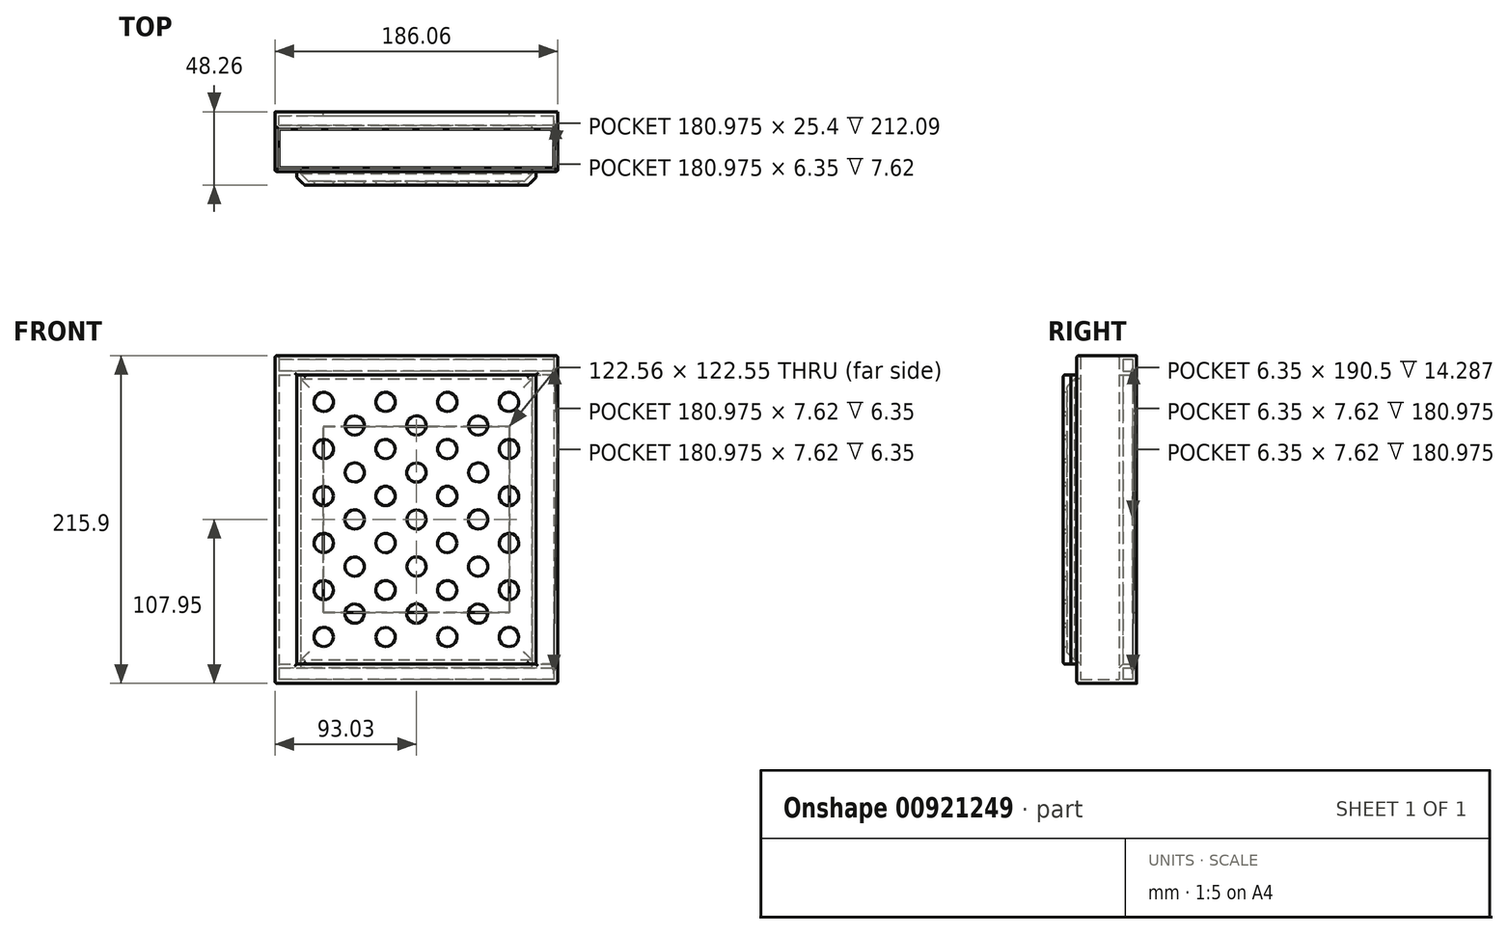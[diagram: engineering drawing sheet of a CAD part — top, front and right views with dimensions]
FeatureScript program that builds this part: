
annotation { "Feature Type Name" : "Feature", "Feature Type Description" : "" }
export const myFeature = defineFeature(function(context is Context, id is Id, definition is map)
    precondition{}
    {
        {
            var Q0;
            Q0=qCreatedBy(makeId("Top.planeOp"),FACE);
            var sketch = newSketch(context, id + "F0", { "sketchPlane" : qUnion([Q0])});
            skLineSegment(sketch, "E0.left", {"start": v(-93.03, 45.72) * mm, "end": v(-93.03, 34.29) * mm});
            skLineSegment(sketch, "E0.right", {"start": v(93.03, 45.72) * mm, "end": v(93.03, 34.29) * mm});
            skLineSegment(sketch, "E1.bottom", {"start": v(-93.03, 34.29) * mm, "end": v(-90.49, 34.29) * mm});
            skLineSegment(sketch, "E1.top", {"start": v(-93.03, 6.35) * mm, "end": v(-90.49, 6.35) * mm});
            skLineSegment(sketch, "E1.left", {"start": v(-93.03, 34.29) * mm, "end": v(-93.03, 6.35) * mm});
            skLineSegment(sketch, "E1.right", {"start": v(-90.49, 34.29) * mm, "end": v(-90.49, 6.35) * mm});
            skLineSegment(sketch, "E2.bottom", {"start": v(93.03, 34.29) * mm, "end": v(90.49, 34.29) * mm});
            skLineSegment(sketch, "E2.top", {"start": v(93.03, 6.35) * mm, "end": v(90.49, 6.35) * mm});
            skLineSegment(sketch, "E2.left", {"start": v(93.03, 34.29) * mm, "end": v(93.03, 6.35) * mm});
            skLineSegment(sketch, "E2.right", {"start": v(90.49, 34.29) * mm, "end": v(90.49, 6.35) * mm});
            skLineSegment(sketch, "E3.bottom", {"start": v(-90.49, 6.35) * mm, "end": v(-76.2, 6.35) * mm});
            skLineSegment(sketch, "E3.top", {"start": v(-90.49, 8.89) * mm, "end": v(-76.2, 8.89) * mm});
            skLineSegment(sketch, "E3.left", {"start": v(-90.49, 6.35) * mm, "end": v(-90.49, 8.89) * mm});
            skLineSegment(sketch, "E3.right", {"start": v(-76.2, 6.35) * mm, "end": v(-76.2, 8.89) * mm});
            skLineSegment(sketch, "E4.bottom", {"start": v(90.49, 6.35) * mm, "end": v(76.2, 6.35) * mm});
            skLineSegment(sketch, "E4.top", {"start": v(90.49, 8.89) * mm, "end": v(76.2, 8.89) * mm});
            skLineSegment(sketch, "E4.left", {"start": v(90.49, 6.35) * mm, "end": v(90.49, 8.89) * mm});
            skLineSegment(sketch, "E4.right", {"start": v(76.2, 6.35) * mm, "end": v(76.2, 8.89) * mm});
            skLineSegment(sketch, "E5", {"start": v(-93.03, 45.72) * mm, "end": v(93.03, 45.72) * mm});
            skLineSegment(sketch, "E6.bottom", {"start": v(-93.03, 34.29) * mm, "end": v(-76.2, 34.29) * mm});
            skLineSegment(sketch, "E6.top", {"start": v(-93.03, 36.83) * mm, "end": v(-76.2, 36.83) * mm});
            skLineSegment(sketch, "E6.left", {"start": v(-93.03, 34.29) * mm, "end": v(-93.03, 36.83) * mm});
            skLineSegment(sketch, "E6.right", {"start": v(-76.2, 34.29) * mm, "end": v(-76.2, 36.83) * mm});
            skLineSegment(sketch, "E7.bottom", {"start": v(93.03, 34.29) * mm, "end": v(76.2, 34.29) * mm});
            skLineSegment(sketch, "E7.top", {"start": v(93.03, 36.83) * mm, "end": v(76.2, 36.83) * mm});
            skLineSegment(sketch, "E7.left", {"start": v(93.03, 34.29) * mm, "end": v(93.03, 36.83) * mm});
            skLineSegment(sketch, "E7.right", {"start": v(76.2, 34.29) * mm, "end": v(76.2, 36.83) * mm});
            skLineSegment(sketch, "E8.bottom", {"start": v(-93.03, 36.83) * mm, "end": v(-90.49, 36.83) * mm});
            skLineSegment(sketch, "E8.top", {"start": v(-93.03, 45.72) * mm, "end": v(-90.49, 45.72) * mm});
            skLineSegment(sketch, "E8.left", {"start": v(-93.03, 36.83) * mm, "end": v(-93.03, 45.72) * mm});
            skLineSegment(sketch, "E8.right", {"start": v(-90.49, 36.83) * mm, "end": v(-90.49, 45.72) * mm});
            skLineSegment(sketch, "E9.bottom", {"start": v(93.03, 36.83) * mm, "end": v(90.49, 36.83) * mm});
            skLineSegment(sketch, "E9.top", {"start": v(93.03, 45.72) * mm, "end": v(90.49, 45.72) * mm});
            skLineSegment(sketch, "E9.left", {"start": v(93.03, 36.83) * mm, "end": v(93.03, 45.72) * mm});
            skLineSegment(sketch, "E9.right", {"start": v(90.49, 36.83) * mm, "end": v(90.49, 45.72) * mm});
            skLineSegment(sketch, "E10.top", {"start": v(-93.03, 43.18) * mm, "end": v(93.03, 43.18) * mm});
            skLineSegment(sketch, "E10.left", {"start": v(-93.03, 45.72) * mm, "end": v(-93.03, 43.18) * mm});
            skLineSegment(sketch, "E10.right", {"start": v(93.03, 45.72) * mm, "end": v(93.03, 43.18) * mm});
            skLineSegment(sketch, "E11.bottom", {"start": v(-76.2, 6.35) * mm, "end": v(-78.74, 6.35) * mm});
            skLineSegment(sketch, "E11.top", {"start": v(-76.2, -2.54) * mm, "end": v(-78.74, -2.54) * mm});
            skLineSegment(sketch, "E11.left", {"start": v(-76.2, 6.35) * mm, "end": v(-76.2, -2.54) * mm});
            skLineSegment(sketch, "E11.right", {"start": v(-78.74, 6.35) * mm, "end": v(-78.74, -2.54) * mm});
            skLineSegment(sketch, "E12.bottom", {"start": v(76.2, 6.35) * mm, "end": v(78.74, 6.35) * mm});
            skLineSegment(sketch, "E12.top", {"start": v(76.2, -2.54) * mm, "end": v(78.74, -2.54) * mm});
            skLineSegment(sketch, "E12.left", {"start": v(76.2, 6.35) * mm, "end": v(76.2, -2.54) * mm});
            skLineSegment(sketch, "E12.right", {"start": v(78.74, 6.35) * mm, "end": v(78.74, -2.54) * mm});
            skLineSegment(sketch, "E13.bottom", {"start": v(-76.2, -2.54) * mm, "end": v(76.2, -2.54) * mm});
            skLineSegment(sketch, "E13.top", {"start": v(-76.2, 0) * mm, "end": v(76.2, 0) * mm});
            skLineSegment(sketch, "E13.left", {"start": v(-76.2, -2.54) * mm, "end": v(-76.2, 0) * mm});
            skLineSegment(sketch, "E13.right", {"start": v(76.2, -2.54) * mm, "end": v(76.2, 0) * mm});
            skPoint(sketch, "E14", {"position": v(0, 0) * mm});
            skLineSegment(sketch, "E15.bottom", {"start": v(-76.2, 36.83) * mm, "end": v(-78.74, 36.83) * mm});
            skLineSegment(sketch, "E15.top", {"start": v(-76.2, 45.72) * mm, "end": v(-78.74, 45.72) * mm});
            skLineSegment(sketch, "E15.left", {"start": v(-76.2, 36.83) * mm, "end": v(-76.2, 45.72) * mm});
            skLineSegment(sketch, "E15.right", {"start": v(-78.74, 36.83) * mm, "end": v(-78.74, 45.72) * mm});
            skLineSegment(sketch, "E16.bottom", {"start": v(76.2, 36.83) * mm, "end": v(78.74, 36.83) * mm});
            skLineSegment(sketch, "E16.top", {"start": v(76.2, 45.72) * mm, "end": v(78.74, 45.72) * mm});
            skLineSegment(sketch, "E16.left", {"start": v(76.2, 36.83) * mm, "end": v(76.2, 45.72) * mm});
            skLineSegment(sketch, "E16.right", {"start": v(78.74, 36.83) * mm, "end": v(78.74, 45.72) * mm});
            skSolve(sketch);
        }
        {
            var Q0;
            Q0 = qSketchRegion(id + "F0", true);
            var Q1;
            {var subQ5=sQuery(id+"F0.wireOp",EDGE,"E16.bottom");Q1=makeQuery(id+"F0.imprint","IMPRINT",FACE,{"disambiguationData":[TD([[makeQuery(id+"F0.imprint","IMPRINT",EDGE,{"derivedFrom":subQ5}),1.0]])]});}
            var Q2;
            {var subQ5=sQuery(id+"F0.wireOp",EDGE,"E15.bottom");Q2=makeQuery(id+"F0.imprint","IMPRINT",FACE,{"disambiguationData":[TD([[makeQuery(id+"F0.imprint","IMPRINT",EDGE,{"derivedFrom":subQ5}),-1.0]])]});}
            extrude(context, id + "F1", {"entities" : qUnion([Q0, Q1, Q2]), "depth" : 215.9 * mm, "offsetDistance" : 25.4 * mm});
        }
        {
            var Q0;
            Q0=makeQuery(id+"F1.opExtrude","SWEPT_FACE",FACE,{"disambiguationData":[OSD([sQuery(id+"F0.wireOp",EDGE,"E5")])]});
            var sketch = newSketch(context, id + "F2", { "sketchPlane" : qUnion([Q0])});
            skPoint(sketch, "E17.centerSnap0", {"position": v(93.03, 107.95) * mm});
            skLineSegment(sketch, "E18.bottom", {"start": v(-61.28, 169.23) * mm, "end": v(61.28, 169.23) * mm});
            skLineSegment(sketch, "E18.top", {"start": v(-61.28, 46.67) * mm, "end": v(61.28, 46.67) * mm});
            skLineSegment(sketch, "E18.left", {"start": v(-61.28, 169.23) * mm, "end": v(-61.28, 46.67) * mm});
            skLineSegment(sketch, "E18.right", {"start": v(61.28, 169.23) * mm, "end": v(61.28, 46.67) * mm});
            skPoint(sketch, "E18.middle", {"position": v(0, 107.95) * mm});
            skSolve(sketch);
        }
        {
            var Q0;
            Q0 = qSketchRegion(id + "F2", true);
            extrude(context, id + "F3", {"entities" : qUnion([Q0]), "operationType" : NewBodyOperationType.REMOVE, "endBound" : BoundingType.UP_TO_NEXT, "oppositeDirection" : true, "depth" : 25.4 * mm, "offsetDistance" : 25.4 * mm});
        }
        {
            var Q0;
            Q0=makeQuery(id+"F1.opExtrude","SWEPT_FACE",FACE,{"disambiguationData":[OSD([sQuery(id+"F0.wireOp",EDGE,"E1.left"),sQuery(id+"F0.wireOp",EDGE,"E6.left"),sQuery(id+"F0.wireOp",EDGE,"E8.left"),sQuery(id+"F0.wireOp",EDGE,"E10.left")])]});
            var sketch = newSketch(context, id + "F4", { "sketchPlane" : qUnion([Q0])});
            skLineSegment(sketch, "E19.bottom", {"start": v(-45.72, 215.9) * mm, "end": v(-34.29, 215.9) * mm});
            skLineSegment(sketch, "E19.top", {"start": v(-45.72, 213.36) * mm, "end": v(-34.29, 213.36) * mm});
            skLineSegment(sketch, "E19.left", {"start": v(-45.72, 215.9) * mm, "end": v(-45.72, 213.36) * mm});
            skLineSegment(sketch, "E19.right", {"start": v(-34.29, 215.9) * mm, "end": v(-34.29, 213.36) * mm});
            skLineSegment(sketch, "E20.bottom", {"start": v(-45.72, 0) * mm, "end": v(-6.35, 0) * mm});
            skLineSegment(sketch, "E20.top", {"start": v(-45.72, 2.54) * mm, "end": v(-6.35, 2.54) * mm});
            skLineSegment(sketch, "E20.left", {"start": v(-45.72, 0) * mm, "end": v(-45.72, 2.54) * mm});
            skLineSegment(sketch, "E20.right", {"start": v(-6.35, 0) * mm, "end": v(-6.35, 2.54) * mm});
            skLineSegment(sketch, "E21.bottom", {"start": v(-6.35, 215.9) * mm, "end": v(-8.89, 215.9) * mm});
            skLineSegment(sketch, "E21.top", {"start": v(-6.35, 203.2) * mm, "end": v(-8.89, 203.2) * mm});
            skLineSegment(sketch, "E21.left", {"start": v(-6.35, 215.9) * mm, "end": v(-6.35, 203.2) * mm});
            skLineSegment(sketch, "E21.right", {"start": v(-8.89, 215.9) * mm, "end": v(-8.89, 203.2) * mm});
            skLineSegment(sketch, "E22.bottom", {"start": v(-6.35, 0) * mm, "end": v(-8.89, 0) * mm});
            skLineSegment(sketch, "E22.top", {"start": v(-6.35, 12.7) * mm, "end": v(-8.89, 12.7) * mm});
            skLineSegment(sketch, "E22.left", {"start": v(-6.35, 0) * mm, "end": v(-6.35, 12.7) * mm});
            skLineSegment(sketch, "E22.right", {"start": v(-8.89, 0) * mm, "end": v(-8.89, 12.7) * mm});
            skLineSegment(sketch, "E23.bottom", {"start": v(-34.29, 215.9) * mm, "end": v(-36.83, 215.9) * mm});
            skLineSegment(sketch, "E23.top", {"start": v(-34.29, 203.2) * mm, "end": v(-36.83, 203.2) * mm});
            skLineSegment(sketch, "E23.left", {"start": v(-34.29, 215.9) * mm, "end": v(-34.29, 203.2) * mm});
            skLineSegment(sketch, "E23.right", {"start": v(-36.83, 215.9) * mm, "end": v(-36.83, 203.2) * mm});
            skLineSegment(sketch, "E24.bottom", {"start": v(-34.29, 0) * mm, "end": v(-36.83, 0) * mm});
            skLineSegment(sketch, "E24.top", {"start": v(-34.29, 12.7) * mm, "end": v(-36.83, 12.7) * mm});
            skLineSegment(sketch, "E24.left", {"start": v(-34.29, 0) * mm, "end": v(-34.29, 12.7) * mm});
            skLineSegment(sketch, "E24.right", {"start": v(-36.83, 0) * mm, "end": v(-36.83, 12.7) * mm});
            skLineSegment(sketch, "E25.bottom", {"start": v(-36.83, 203.2) * mm, "end": v(-45.72, 203.2) * mm});
            skLineSegment(sketch, "E25.top", {"start": v(-36.83, 205.74) * mm, "end": v(-45.72, 205.74) * mm});
            skLineSegment(sketch, "E25.left", {"start": v(-36.83, 203.2) * mm, "end": v(-36.83, 205.74) * mm});
            skLineSegment(sketch, "E25.right", {"start": v(-45.72, 203.2) * mm, "end": v(-45.72, 205.74) * mm});
            skLineSegment(sketch, "E26.bottom", {"start": v(-36.83, 12.7) * mm, "end": v(-45.72, 12.7) * mm});
            skLineSegment(sketch, "E26.top", {"start": v(-36.83, 10.16) * mm, "end": v(-45.72, 10.16) * mm});
            skLineSegment(sketch, "E26.left", {"start": v(-36.83, 12.7) * mm, "end": v(-36.83, 10.16) * mm});
            skLineSegment(sketch, "E26.right", {"start": v(-45.72, 12.7) * mm, "end": v(-45.72, 10.16) * mm});
            skSolve(sketch);
        }
        {
            var Q0;
            Q0 = qSketchRegion(id + "F4", true);
            var Q1;
            Q1=makeQuery(id+"F1.opExtrude","SWEPT_FACE",FACE,{"disambiguationData":[OSD([sQuery(id+"F0.wireOp",EDGE,"E2.left"),sQuery(id+"F0.wireOp",EDGE,"E7.left"),sQuery(id+"F0.wireOp",EDGE,"E9.left"),sQuery(id+"F0.wireOp",EDGE,"E10.right")])]});
            extrude(context, id + "F5", {"entities" : qUnion([Q0]), "operationType" : NewBodyOperationType.ADD, "endBound" : BoundingType.UP_TO_SURFACE, "oppositeDirection" : true, "depth" : 25.4 * mm, "endBoundEntityFace" : qUnion([Q1]), "offsetDistance" : 25.4 * mm});
        }
        {
            var Q0;
            Q0=makeQuery(id+"F1.opExtrude","SWEPT_FACE",FACE,{"disambiguationData":[OSD([sQuery(id+"F0.wireOp",EDGE,"E12.right")])]});
            var sketch = newSketch(context, id + "F6", { "sketchPlane" : qUnion([Q0])});
            skLineSegment(sketch, "E27.bottom", {"start": v(-2.54, 0) * mm, "end": v(6.35, 0) * mm});
            skLineSegment(sketch, "E27.top", {"start": v(-2.54, 12.7) * mm, "end": v(6.35, 12.7) * mm});
            skLineSegment(sketch, "E27.left", {"start": v(-2.54, 0) * mm, "end": v(-2.54, 12.7) * mm});
            skLineSegment(sketch, "E27.right", {"start": v(6.35, 0) * mm, "end": v(6.35, 12.7) * mm});
            skLineSegment(sketch, "E28.bottom", {"start": v(-2.54, 215.9) * mm, "end": v(6.35, 215.9) * mm});
            skLineSegment(sketch, "E28.top", {"start": v(-2.54, 203.2) * mm, "end": v(6.35, 203.2) * mm});
            skLineSegment(sketch, "E28.left", {"start": v(-2.54, 215.9) * mm, "end": v(-2.54, 203.2) * mm});
            skLineSegment(sketch, "E28.right", {"start": v(6.35, 215.9) * mm, "end": v(6.35, 203.2) * mm});
            skSolve(sketch);
        }
        {
            var Q0;
            Q0 = qSketchRegion(id + "F6", true);
            var Q1;
            Q1=makeQuery(id+"F1.opExtrude","SWEPT_FACE",FACE,{"disambiguationData":[OSD([sQuery(id+"F0.wireOp",EDGE,"E11.right")])]});
            extrude(context, id + "F7", {"entities" : qUnion([Q0]), "operationType" : NewBodyOperationType.REMOVE, "endBound" : BoundingType.UP_TO_SURFACE, "oppositeDirection" : true, "depth" : 25.4 * mm, "endBoundEntityFace" : qUnion([Q1]), "offsetDistance" : 25.4 * mm});
        }
        {
            var Q0;
            Q0=makeQuery(id+"F1.opExtrude","SWEPT_FACE",FACE,{"disambiguationData":[OSD([sQuery(id+"F0.wireOp",EDGE,"E12.right")])]});
            var sketch = newSketch(context, id + "F8", { "sketchPlane" : qUnion([Q0])});
            skLineSegment(sketch, "E29.bottom", {"start": v(-2.54, 12.7) * mm, "end": v(8.89, 12.7) * mm});
            skLineSegment(sketch, "E29.top", {"start": v(-2.54, 15.24) * mm, "end": v(8.89, 15.24) * mm});
            skLineSegment(sketch, "E29.left", {"start": v(-2.54, 12.7) * mm, "end": v(-2.54, 15.24) * mm});
            skLineSegment(sketch, "E29.right", {"start": v(8.89, 12.7) * mm, "end": v(8.89, 15.24) * mm});
            skLineSegment(sketch, "E30.bottom", {"start": v(-2.54, 203.2) * mm, "end": v(8.89, 203.2) * mm});
            skLineSegment(sketch, "E30.top", {"start": v(-2.54, 200.66) * mm, "end": v(8.89, 200.66) * mm});
            skLineSegment(sketch, "E30.left", {"start": v(-2.54, 203.2) * mm, "end": v(-2.54, 200.66) * mm});
            skLineSegment(sketch, "E30.right", {"start": v(8.89, 203.2) * mm, "end": v(8.89, 200.66) * mm});
            skSolve(sketch);
        }
        {
            var Q0;
            Q0 = qSketchRegion(id + "F8", true);
            var Q1;
            Q1=makeQuery(id+"F1.opExtrude","SWEPT_FACE",FACE,{"disambiguationData":[OSD([sQuery(id+"F0.wireOp",EDGE,"E11.right")])]});
            extrude(context, id + "F9", {"entities" : qUnion([Q0]), "operationType" : NewBodyOperationType.ADD, "endBound" : BoundingType.UP_TO_SURFACE, "oppositeDirection" : true, "depth" : 25.4 * mm, "endBoundEntityFace" : qUnion([Q1]), "offsetDistance" : 25.4 * mm});
        }
        {
            var Q0;
            Q0=makeQuery(id+"F7.boolean.opBoolean","COPY",EDGE,{"derivedFrom":makeQuery(id+"F7.opExtrude","SWEPT_EDGE",EDGE,{"disambiguationData":[OSD([sQuery(id+"F0.wireOp",EDGE,"E12.top"),sQuery(id+"F0.wireOp",EDGE,"E12.right"),sQuery(id+"F6.wireOp",EDGE,"E28.top"),sQuery(id+"F6.wireOp",EDGE,"E28.left")])]})});
            var Q1;
            Q1=makeQuery(id+"F1.opExtrude","SWEPT_EDGE",EDGE,{"disambiguationData":[OSD([sQuery(id+"F0.wireOp",EDGE,"E12.top"),sQuery(id+"F0.wireOp",EDGE,"E12.right")])]});
            var Q2;
            Q2=makeQuery(id+"F1.opExtrude","SWEPT_EDGE",EDGE,{"disambiguationData":[OSD([sQuery(id+"F0.wireOp",EDGE,"E11.top"),sQuery(id+"F0.wireOp",EDGE,"E11.right")])]});
            var Q3;
            Q3=makeQuery(id+"F7.boolean.opBoolean","COPY",EDGE,{"derivedFrom":makeQuery(id+"F7.opExtrude","SWEPT_EDGE",EDGE,{"disambiguationData":[OSD([sQuery(id+"F0.wireOp",EDGE,"E12.top"),sQuery(id+"F0.wireOp",EDGE,"E12.right"),sQuery(id+"F6.wireOp",EDGE,"E27.top"),sQuery(id+"F6.wireOp",EDGE,"E27.left")])]})});
            var Q4;
            Q4=makeQuery(id+"F9.boolean.opBoolean","INTERSECT",EDGE,{"derivedFrom":[makeQuery(id+"F1.opExtrude","SWEPT_FACE",FACE,{"disambiguationData":[OSD([sQuery(id+"F0.wireOp",EDGE,"E13.top")])]}),makeQuery(id+"F9.opExtrude","SWEPT_FACE",FACE,{"disambiguationData":[OSD([sQuery(id+"F8.wireOp",EDGE,"E30.top")])]})]});
            var Q5;
            Q5=makeQuery(id+"F1.opExtrude","SWEPT_EDGE",EDGE,{"disambiguationData":[OSD([sQuery(id+"F0.wireOp",EDGE,"E11.left"),sQuery(id+"F0.wireOp",EDGE,"E13.top"),sQuery(id+"F0.wireOp",EDGE,"E13.left")])]});
            var Q6;
            Q6=makeQuery(id+"F9.boolean.opBoolean","INTERSECT",EDGE,{"derivedFrom":[makeQuery(id+"F1.opExtrude","SWEPT_FACE",FACE,{"disambiguationData":[OSD([sQuery(id+"F0.wireOp",EDGE,"E13.top")])]}),makeQuery(id+"F9.opExtrude","SWEPT_FACE",FACE,{"disambiguationData":[OSD([sQuery(id+"F8.wireOp",EDGE,"E29.top")])]})]});
            var Q7;
            Q7=makeQuery(id+"F1.opExtrude","SWEPT_EDGE",EDGE,{"disambiguationData":[OSD([sQuery(id+"F0.wireOp",EDGE,"E12.left"),sQuery(id+"F0.wireOp",EDGE,"E13.top"),sQuery(id+"F0.wireOp",EDGE,"E13.right")])]});
            chamfer(context, id + "F10", {"entities" : qUnion([Q0, Q1, Q2, Q3, Q4, Q5, Q6, Q7]), "width" : 5.08 * mm, "tangentPropagation" : true});
        }
        {
            var Q0;
            Q0=makeQuery(id+"F7.boolean.opBoolean","MERGE",FACE,{"derivedFrom":[makeQuery(id+"F1.opExtrude","SWEPT_FACE",FACE,{"disambiguationData":[OSD([sQuery(id+"F0.wireOp",EDGE,"E1.top"),sQuery(id+"F0.wireOp",EDGE,"E3.bottom")])]}),makeQuery(id+"F1.opExtrude","SWEPT_FACE",FACE,{"disambiguationData":[OSD([sQuery(id+"F0.wireOp",EDGE,"E2.top"),sQuery(id+"F0.wireOp",EDGE,"E4.bottom")])]}),makeQuery(id+"F5.opExtrude","SWEPT_FACE",FACE,{"disambiguationData":[OSD([sQuery(id+"F4.wireOp",EDGE,"E21.left")])]}),makeQuery(id+"F5.opExtrude","SWEPT_FACE",FACE,{"disambiguationData":[OSD([sQuery(id+"F4.wireOp",EDGE,"E22.left")])]})],"fromTools":[makeQuery(id+"F7.opExtrude","SWEPT_FACE",FACE,{"disambiguationData":[OSD([sQuery(id+"F6.wireOp",EDGE,"E27.right")])]}),makeQuery(id+"F7.opExtrude","SWEPT_FACE",FACE,{"disambiguationData":[OSD([sQuery(id+"F6.wireOp",EDGE,"E28.right")])]})]});
            var Q1;
            Q1=makeQuery(id+"F3.boolean.opBoolean","COPY",FACE,{"disambiguationData":[TD([makeQuery(id+"F1.opExtrude","SWEPT_FACE",FACE,{"disambiguationData":[OSD([sQuery(id+"F0.wireOp",EDGE,"E13.top")])]})])],"derivedFrom":makeQuery(id+"F3.opExtrude","SWEPT_FACE",FACE,{"disambiguationData":[OSD([sQuery(id+"F2.wireOp",EDGE,"E17")])]})});
            var Q2;
            {var subQ0=sQuery(id+"F0.wireOp",EDGE,"E10.top");Q2=makeQuery(id+"F3.boolean.opBoolean","COPY",FACE,{"disambiguationData":[TD([makeQuery(id+"F1.opExtrude","SWEPT_FACE",FACE,{"disambiguationData":[OSD([subQ0]),TDD([makeQuery(id+"F0.imprint","IMPRINT",EDGE,{"disambiguationData":[TD([[makeQuery(id+"F0.imprint","INTERSECT",VERTEX,{"derivedFrom":[subQ0,sQuery(id+"F0.wireOp",EDGE,"E15.left")]}),-1.0]])],"derivedFrom":subQ0})])]})])],"derivedFrom":makeQuery(id+"F3.opExtrude","SWEPT_FACE",FACE,{"disambiguationData":[OSD([sQuery(id+"F2.wireOp",EDGE,"E17")])]})});}
            var Q3;
            Q3=makeQuery(id+"F1.opExtrude","CAP_EDGE",EDGE,{"disambiguationData":[OSD([sQuery(id+"F0.wireOp",EDGE,"E1.left"),sQuery(id+"F0.wireOp",EDGE,"E6.left"),sQuery(id+"F0.wireOp",EDGE,"E8.left"),sQuery(id+"F0.wireOp",EDGE,"E10.left")])],"isStart":false});
            var Q4;
            Q4=makeQuery(id+"F1.opExtrude","CAP_EDGE",EDGE,{"disambiguationData":[OSD([sQuery(id+"F0.wireOp",EDGE,"E1.left"),sQuery(id+"F0.wireOp",EDGE,"E6.left"),sQuery(id+"F0.wireOp",EDGE,"E8.left"),sQuery(id+"F0.wireOp",EDGE,"E10.left")])],"isStart":true});
            var Q5;
            Q5=makeQuery(id+"F1.opExtrude","CAP_EDGE",EDGE,{"disambiguationData":[OSD([sQuery(id+"F0.wireOp",EDGE,"E2.left"),sQuery(id+"F0.wireOp",EDGE,"E7.left"),sQuery(id+"F0.wireOp",EDGE,"E9.left"),sQuery(id+"F0.wireOp",EDGE,"E10.right")])],"isStart":false});
            var Q6;
            Q6=makeQuery(id+"F1.opExtrude","CAP_EDGE",EDGE,{"disambiguationData":[OSD([sQuery(id+"F0.wireOp",EDGE,"E2.left"),sQuery(id+"F0.wireOp",EDGE,"E7.left"),sQuery(id+"F0.wireOp",EDGE,"E9.left"),sQuery(id+"F0.wireOp",EDGE,"E10.right")])],"isStart":true});
            var Q7;
            Q7=makeQuery(id+"F5.boolean.opBoolean","MERGE",EDGE,{"derivedFrom":[makeQuery(id+"F1.opExtrude","CAP_EDGE",EDGE,{"disambiguationData":[OSD([sQuery(id+"F0.wireOp",EDGE,"E6.bottom")])],"isStart":false}),makeQuery(id+"F1.opExtrude","CAP_EDGE",EDGE,{"disambiguationData":[OSD([sQuery(id+"F0.wireOp",EDGE,"E7.bottom")])],"isStart":false}),makeQuery(id+"F5.opExtrude","SWEPT_EDGE",EDGE,{"disambiguationData":[OSD([sQuery(id+"F0.wireOp",EDGE,"E1.left"),sQuery(id+"F0.wireOp",EDGE,"E6.left"),sQuery(id+"F0.wireOp",EDGE,"E8.left"),sQuery(id+"F0.wireOp",EDGE,"E10.left"),sQuery(id+"F4.wireOp",EDGE,"E23.bottom"),sQuery(id+"F4.wireOp",EDGE,"E23.left")])]})]});
            var Q8;
            Q8=makeQuery(id+"F5.boolean.opBoolean","MERGE",EDGE,{"derivedFrom":[makeQuery(id+"F1.opExtrude","CAP_EDGE",EDGE,{"disambiguationData":[OSD([sQuery(id+"F0.wireOp",EDGE,"E3.top")])],"isStart":false}),makeQuery(id+"F1.opExtrude","CAP_EDGE",EDGE,{"disambiguationData":[OSD([sQuery(id+"F0.wireOp",EDGE,"E4.top")])],"isStart":false}),makeQuery(id+"F5.opExtrude","SWEPT_EDGE",EDGE,{"disambiguationData":[OSD([sQuery(id+"F0.wireOp",EDGE,"E1.left"),sQuery(id+"F0.wireOp",EDGE,"E6.left"),sQuery(id+"F0.wireOp",EDGE,"E8.left"),sQuery(id+"F0.wireOp",EDGE,"E10.left"),sQuery(id+"F4.wireOp",EDGE,"E21.bottom"),sQuery(id+"F4.wireOp",EDGE,"E21.right")])]})]});
            var Q9;
            Q9=makeQuery(id+"F1.opExtrude","CAP_EDGE",EDGE,{"disambiguationData":[OSD([sQuery(id+"F0.wireOp",EDGE,"E1.right")])],"isStart":false});
            var Q10;
            Q10=makeQuery(id+"F1.opExtrude","CAP_EDGE",EDGE,{"disambiguationData":[OSD([sQuery(id+"F0.wireOp",EDGE,"E2.right")])],"isStart":false});
            fillet(context, id + "F11", {"entities" : qUnion([Q0, Q1, Q2, Q3, Q4, Q5, Q6, Q7, Q8, Q9, Q10]), "radius" : 1.27 * mm, "tangentPropagation" : true, "allowEdgeOverflow" : false});
        }
        {
            var Q0;
            Q0=makeQuery(id+"F5.opExtrude","SWEPT_EDGE",EDGE,{"disambiguationData":[OSD([sQuery(id+"F4.wireOp",EDGE,"E24.top"),sQuery(id+"F4.wireOp",EDGE,"E24.left")])]});
            var Q1;
            Q1=makeQuery(id+"F9.opExtrude","SWEPT_EDGE",EDGE,{"disambiguationData":[OSD([sQuery(id+"F8.wireOp",EDGE,"E29.top"),sQuery(id+"F8.wireOp",EDGE,"E29.right")])]});
            chamfer(context, id + "F12", {"entities" : qUnion([Q0, Q1]), "width" : 2.54 * mm, "tangentPropagation" : true});
        }
        {
            var Q0;
            Q0=makeQuery(id+"F1.opExtrude","SWEPT_FACE",FACE,{"disambiguationData":[OSD([sQuery(id+"F0.wireOp",EDGE,"E11.top"),sQuery(id+"F0.wireOp",EDGE,"E12.top"),sQuery(id+"F0.wireOp",EDGE,"E13.bottom")])]});
            var sketch = newSketch(context, id + "F13", { "sketchPlane" : qUnion([Q0])});
            skCircle(sketch, "E31", {"center": v(-60.96, 185.42) * mm, "radius": 6.35 * mm});
            skCircle(sketch, "E32.0.1.0", {"center": v(-60.96, 154.43) * mm, "radius": 6.35 * mm});
            skCircle(sketch, "E32.0.2.0", {"center": v(-60.96, 123.44) * mm, "radius": 6.35 * mm});
            skCircle(sketch, "E32.0.3.0", {"center": v(-60.96, 92.46) * mm, "radius": 6.35 * mm});
            skCircle(sketch, "E32.0.4.0", {"center": v(-60.96, 61.47) * mm, "radius": 6.35 * mm});
            skCircle(sketch, "E32.0.5.0", {"center": v(-60.96, 30.48) * mm, "radius": 6.35 * mm});
            skCircle(sketch, "E32.1.0.0", {"center": v(-20.32, 185.42) * mm, "radius": 6.35 * mm});
            skCircle(sketch, "E32.1.1.0", {"center": v(-20.32, 154.43) * mm, "radius": 6.35 * mm});
            skCircle(sketch, "E32.1.2.0", {"center": v(-20.32, 123.44) * mm, "radius": 6.35 * mm});
            skCircle(sketch, "E32.1.3.0", {"center": v(-20.32, 92.46) * mm, "radius": 6.35 * mm});
            skCircle(sketch, "E32.1.4.0", {"center": v(-20.32, 61.47) * mm, "radius": 6.35 * mm});
            skCircle(sketch, "E32.1.5.0", {"center": v(-20.32, 30.48) * mm, "radius": 6.35 * mm});
            skCircle(sketch, "E32.2.0.0", {"center": v(20.32, 185.42) * mm, "radius": 6.35 * mm});
            skCircle(sketch, "E32.2.1.0", {"center": v(20.32, 154.43) * mm, "radius": 6.35 * mm});
            skCircle(sketch, "E32.2.2.0", {"center": v(20.32, 123.44) * mm, "radius": 6.35 * mm});
            skCircle(sketch, "E32.2.3.0", {"center": v(20.32, 92.46) * mm, "radius": 6.35 * mm});
            skCircle(sketch, "E32.2.4.0", {"center": v(20.32, 61.47) * mm, "radius": 6.35 * mm});
            skCircle(sketch, "E32.2.5.0", {"center": v(20.32, 30.48) * mm, "radius": 6.35 * mm});
            skCircle(sketch, "E32.3.0.0", {"center": v(60.96, 185.42) * mm, "radius": 6.35 * mm});
            skCircle(sketch, "E32.3.1.0", {"center": v(60.96, 154.43) * mm, "radius": 6.35 * mm});
            skCircle(sketch, "E32.3.2.0", {"center": v(60.96, 123.44) * mm, "radius": 6.35 * mm});
            skCircle(sketch, "E32.3.3.0", {"center": v(60.96, 92.46) * mm, "radius": 6.35 * mm});
            skCircle(sketch, "E32.3.4.0", {"center": v(60.96, 61.47) * mm, "radius": 6.35 * mm});
            skCircle(sketch, "E32.3.5.0", {"center": v(60.96, 30.48) * mm, "radius": 6.35 * mm});
            skLineSegment(sketch, "E32.direction1", {"start": v(-60.96, 185.42) * mm, "end": v(-20.32, 185.42) * mm, "construction": true});
            skLineSegment(sketch, "E32.direction2", {"start": v(-60.96, 185.42) * mm, "end": v(-60.96, 154.43) * mm, "construction": true});
            skCircle(sketch, "E33", {"center": v(-40.64, 169.93) * mm, "radius": 6.35 * mm});
            skPoint(sketch, "E34", {"position": v(-40.64, 185.42) * mm});
            skPoint(sketch, "E35", {"position": v(-60.96, 169.93) * mm});
            skCircle(sketch, "E36.0.1.0", {"center": v(-40.64, 138.94) * mm, "radius": 6.35 * mm});
            skCircle(sketch, "E36.0.2.0", {"center": v(-40.64, 107.95) * mm, "radius": 6.35 * mm});
            skCircle(sketch, "E36.0.3.0", {"center": v(-40.64, 76.96) * mm, "radius": 6.35 * mm});
            skCircle(sketch, "E36.0.4.0", {"center": v(-40.64, 45.97) * mm, "radius": 6.35 * mm});
            skCircle(sketch, "E36.1.0.0", {"center": v(0, 169.93) * mm, "radius": 6.35 * mm});
            skCircle(sketch, "E36.1.1.0", {"center": v(0, 138.94) * mm, "radius": 6.35 * mm});
            skCircle(sketch, "E36.1.2.0", {"center": v(0, 107.95) * mm, "radius": 6.35 * mm});
            skCircle(sketch, "E36.1.3.0", {"center": v(0, 76.96) * mm, "radius": 6.35 * mm});
            skCircle(sketch, "E36.1.4.0", {"center": v(0, 45.97) * mm, "radius": 6.35 * mm});
            skCircle(sketch, "E36.2.0.0", {"center": v(40.64, 169.93) * mm, "radius": 6.35 * mm});
            skCircle(sketch, "E36.2.1.0", {"center": v(40.64, 138.94) * mm, "radius": 6.35 * mm});
            skCircle(sketch, "E36.2.2.0", {"center": v(40.64, 107.95) * mm, "radius": 6.35 * mm});
            skCircle(sketch, "E36.2.3.0", {"center": v(40.64, 76.96) * mm, "radius": 6.35 * mm});
            skCircle(sketch, "E36.2.4.0", {"center": v(40.64, 45.97) * mm, "radius": 6.35 * mm});
            skLineSegment(sketch, "E36.direction1", {"start": v(-40.64, 169.93) * mm, "end": v(0, 169.93) * mm, "construction": true});
            skLineSegment(sketch, "E36.direction2", {"start": v(-40.64, 169.93) * mm, "end": v(-40.64, 138.94) * mm, "construction": true});
            skLineSegment(sketch, "E37", {"start": v(60.96, 61.47) * mm, "end": v(60.96, 30.48) * mm, "construction": true});
            skLineSegment(sketch, "E38", {"start": v(60.96, 30.48) * mm, "end": v(20.32, 30.48) * mm, "construction": true});
            skPoint(sketch, "E39", {"position": v(40.64, 30.48) * mm});
            skPoint(sketch, "E40", {"position": v(60.96, 45.97) * mm});
            skSolve(sketch);
        }
        {
            var Q0;
            Q0 = qSketchRegion(id + "F13", true);
            extrude(context, id + "F14", {"entities" : qUnion([Q0]), "operationType" : NewBodyOperationType.REMOVE, "endBound" : BoundingType.UP_TO_NEXT, "oppositeDirection" : true, "depth" : 25.4 * mm, "offsetDistance" : 25.4 * mm});
        }
        {
            var Q0;
            Q0=makeQuery(id+"F1.opExtrude","SWEPT_FACE",FACE,{"disambiguationData":[OSD([sQuery(id+"F0.wireOp",EDGE,"E11.top"),sQuery(id+"F0.wireOp",EDGE,"E12.top"),sQuery(id+"F0.wireOp",EDGE,"E13.bottom")])]});
            var Q1;
            Q1=makeQuery(id+"F1.opExtrude","SWEPT_FACE",FACE,{"disambiguationData":[OSD([sQuery(id+"F0.wireOp",EDGE,"E13.top")])]});
            fillet(context, id + "F15", {"entities" : qUnion([Q0, Q1]), "radius" : 1.27 * mm, "tangentPropagation" : true, "allowEdgeOverflow" : false});
        }
    });
